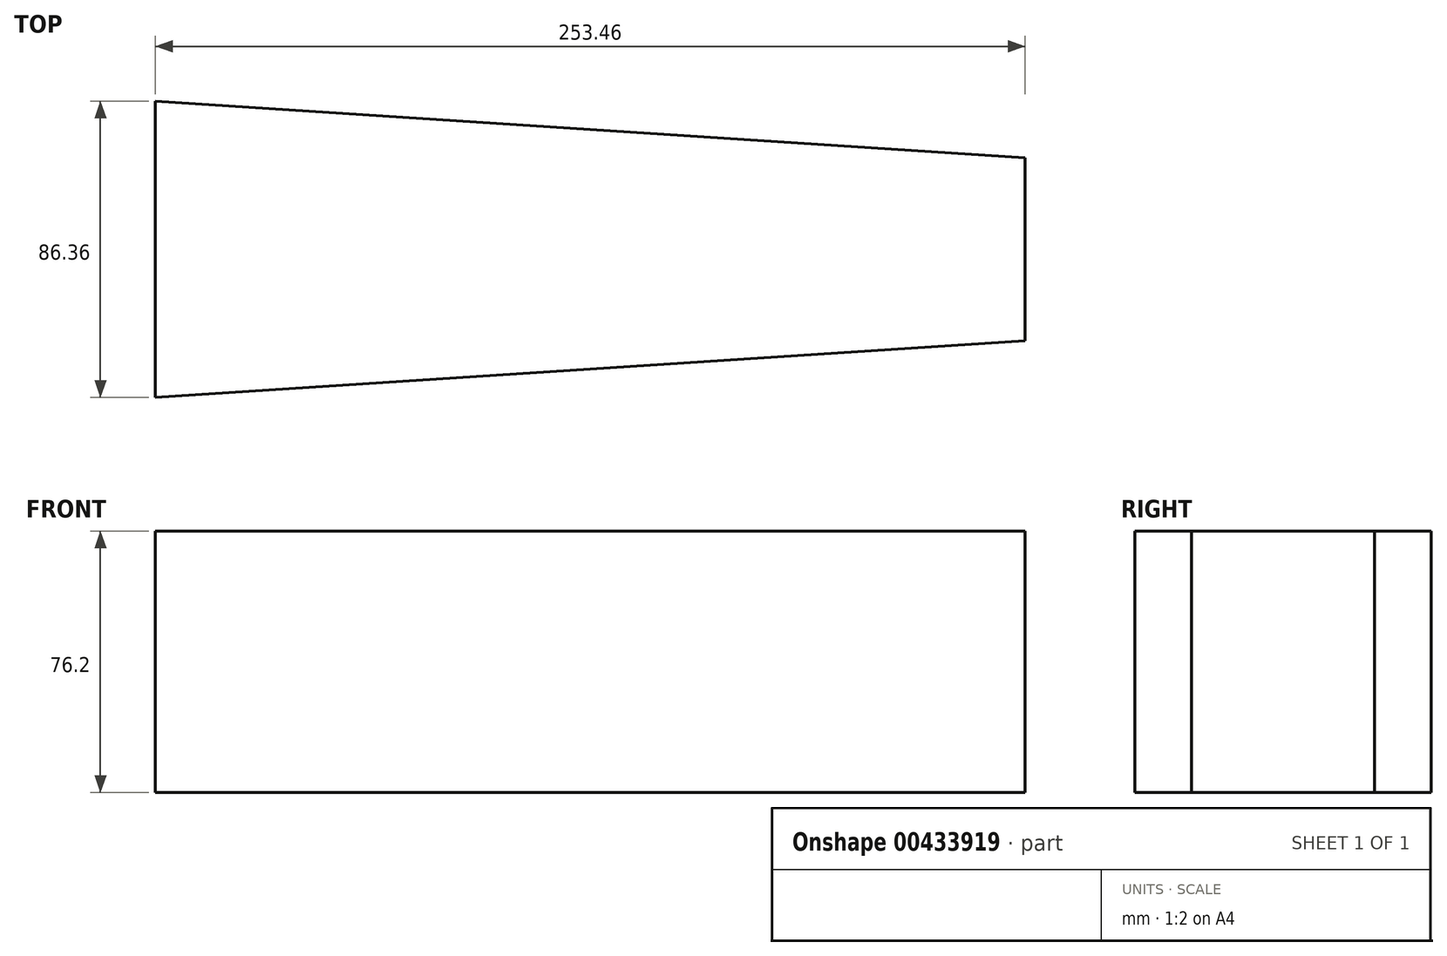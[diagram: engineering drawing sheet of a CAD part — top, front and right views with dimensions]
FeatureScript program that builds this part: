
annotation { "Feature Type Name" : "Feature", "Feature Type Description" : "" }
export const myFeature = defineFeature(function(context is Context, id is Id, definition is map)
    precondition{}
    {
        {
            var Q0;
            Q0=qCreatedBy(makeId("Top.planeOp"),FACE);
            var sketch = newSketch(context, id + "F0", { "sketchPlane" : qUnion([Q0])});
            skLineSegment(sketch, "E0", {"start": v(-207.74, 52.9) * mm, "end": v(-207.74, -33.45) * mm});
            skLineSegment(sketch, "E1", {"start": v(-207.74, -33.45) * mm, "end": v(45.72, -16.94) * mm});
            skLineSegment(sketch, "E2", {"start": v(45.72, -16.94) * mm, "end": v(45.72, 36.4) * mm});
            skLineSegment(sketch, "E3", {"start": v(45.72, 36.4) * mm, "end": v(-207.74, 52.9) * mm});
            skSolve(sketch);
        }
        {
            var Q0;
            Q0=makeQuery(id+"F0.imprint","IMPRINT",FACE,{"disambiguationData":[TD([[makeQuery(id+"F0.imprint","IMPRINT",EDGE,{"derivedFrom":sQuery(id+"F0.wireOp",EDGE,"E0")}),1.0]])]});
            extrude(context, id + "F1", {"entities" : qUnion([Q0]), "depth" : 76.2 * mm});
        }
    });
